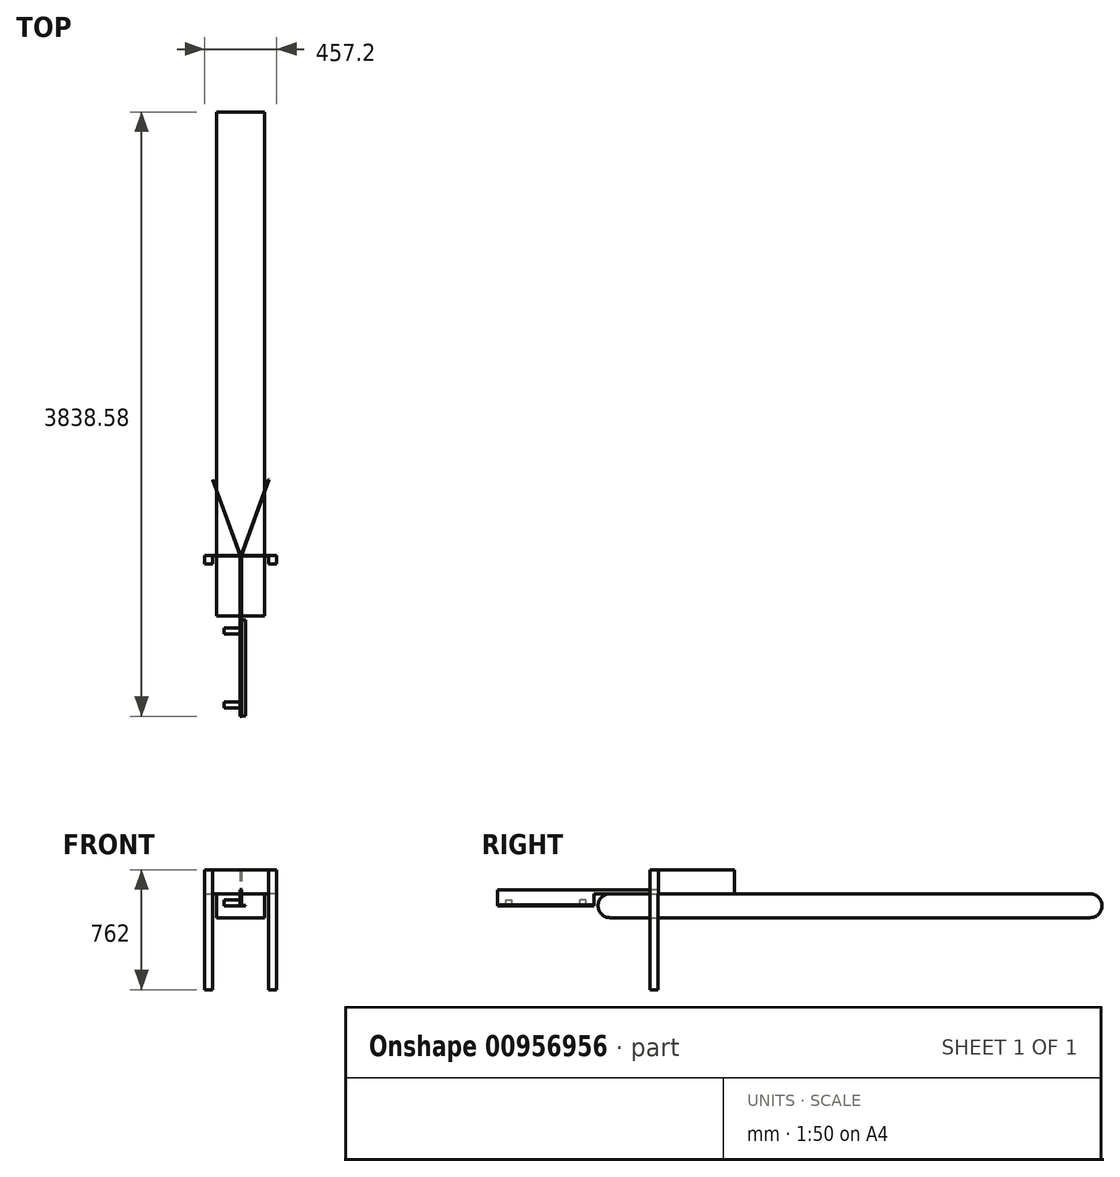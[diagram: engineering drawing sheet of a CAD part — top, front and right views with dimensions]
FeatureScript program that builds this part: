
annotation { "Feature Type Name" : "Feature", "Feature Type Description" : "" }
export const myFeature = defineFeature(function(context is Context, id is Id, definition is map)
    precondition{}
    {
        {
            var Q0;
            Q0=qCreatedBy(makeId("Right.planeOp"),FACE);
            var sketch = newSketch(context, id + "F0", { "sketchPlane" : qUnion([Q0])});
            skLineSegment(sketch, "E0", {"start": v(-1480.5, 76.38) * mm, "end": v(1567.5, 76.38) * mm});
            skLineSegment(sketch, "E1", {"start": v(-1480.5, -76.02) * mm, "end": v(1567.5, -76.02) * mm});
            skArc(sketch, "E2", {"start": v(-1480.5, -76.02) * mm, "mid": v(-1556.7, 0.18) * mm, "end": v(-1480.5, 76.38) * mm});
            skArc(sketch, "E3", {"start": v(1567.5, -76.02) * mm, "mid": v(1643.7, 0.18) * mm, "end": v(1567.5, 76.38) * mm});
            skSolve(sketch);
        }
        {
            var Q0;
            Q0=makeQuery(id+"F0.imprint","IMPRINT",FACE,{"disambiguationData":[TD([[makeQuery(id+"F0.imprint","IMPRINT",EDGE,{"derivedFrom":sQuery(id+"F0.wireOp",EDGE,"E0")}),-1.0]])]});
            extrude(context, id + "F1", {"entities" : qUnion([Q0]), "depth" : 304.8 * mm, "offsetDistance" : 25.4 * mm});
        }
        {
            var Q0;
            Q0=makeQuery(id+"F1.opExtrude","SWEPT_FACE",FACE,{"disambiguationData":[OSD([sQuery(id+"F0.wireOp",EDGE,"E0")])]});
            var sketch = newSketch(context, id + "F2", { "sketchPlane" : qUnion([Q0])});
            skLineSegment(sketch, "E4.bottom", {"start": v(381, -1175.7) * mm, "end": v(152.4, -1175.7) * mm});
            skLineSegment(sketch, "E4.top", {"start": v(381, -1173.4) * mm, "end": v(152.4, -1173.4) * mm});
            skLineSegment(sketch, "E4.left", {"start": v(381, -1175.7) * mm, "end": v(381, -1173.4) * mm});
            skLineSegment(sketch, "E4.right", {"start": v(152.4, -1175.7) * mm, "end": v(152.4, -1173.4) * mm});
            skLineSegment(sketch, "E5", {"start": v(152.4, -1480.5) * mm, "end": v(152.4, 1567.5) * mm, "construction": true});
            skLineSegment(sketch, "E6.bottom", {"start": v(381, -1175.7) * mm, "end": v(330.2, -1175.7) * mm});
            skLineSegment(sketch, "E6.top", {"start": v(381, -1226.5) * mm, "end": v(330.2, -1226.5) * mm});
            skLineSegment(sketch, "E6.left", {"start": v(381, -1175.7) * mm, "end": v(381, -1226.5) * mm});
            skLineSegment(sketch, "E6.right", {"start": v(330.2, -1175.7) * mm, "end": v(330.2, -1226.5) * mm});
            skLineSegment(sketch, "E7", {"start": v(154.43, -1173.4) * mm, "end": v(330.2, -690.49) * mm});
            skLineSegment(sketch, "E8", {"start": v(330.2, -690.49) * mm, "end": v(332.35, -691.27) * mm});
            skLineSegment(sketch, "E9", {"start": v(332.35, -691.27) * mm, "end": v(156.86, -1173.4) * mm});
            skSolve(sketch);
        }
        {
            var Q0;
            {var subQ0=sQuery(id+"F2.wireOp",EDGE,"E4.left");Q0=makeQuery(id+"F2.imprint","IMPRINT",FACE,{"disambiguationData":[TD([[makeQuery(id+"F2.imprint","IMPRINT",EDGE,{"derivedFrom":subQ0}),1.0]])]});}
            var Q1;
            {var subQ5=sQuery(id+"F2.wireOp",EDGE,"E4.right");Q1=makeQuery(id+"F2.imprint","IMPRINT",FACE,{"disambiguationData":[TD([[makeQuery(id+"F2.imprint","IMPRINT",EDGE,{"derivedFrom":subQ5}),-1.0]])]});}
            var Q2;
            {var subQ0=sQuery(id+"F2.wireOp",EDGE,"E8");Q2=makeQuery(id+"F2.imprint","IMPRINT",FACE,{"disambiguationData":[TD([[makeQuery(id+"F2.imprint","IMPRINT",EDGE,{"derivedFrom":subQ0}),-1.0]])]});}
            var Q3;
            {var subQ0=sQuery(id+"F2.wireOp",EDGE,"E7");var subQ1=sQuery(id+"F2.wireOp",EDGE,"E4.top");var subQ2=makeQuery(id+"F2.imprint","INTERSECT",VERTEX,{"derivedFrom":[subQ1,subQ0]});Q3=makeQuery(id+"F2.imprint","IMPRINT",FACE,{"disambiguationData":[TD([[makeQuery(id+"F2.imprint","IMPRINT",EDGE,{"disambiguationData":[TD([[subQ2,1.0]])],"derivedFrom":subQ1}),-1.0]])]});}
            extrude(context, id + "F3", {"entities" : qUnion([Q0, Q1, Q2, Q3]), "operationType" : NewBodyOperationType.ADD, "depth" : 152.4 * mm, "offsetDistance" : 25.4 * mm});
        }
        {
            var Q0;
            Q0=makeQuery(id+"F2.imprint","IMPRINT",FACE,{"disambiguationData":[TD([[makeQuery(id+"F2.imprint","IMPRINT",EDGE,{"derivedFrom":sQuery(id+"F2.wireOp",EDGE,"E6.top")}),-1.0]])]});
            extrude(context, id + "F4", {"entities" : qUnion([Q0]), "operationType" : NewBodyOperationType.ADD, "depth" : 152.4 * mm, "offsetDistance" : 25.4 * mm, "hasSecondDirection" : true, "secondDirectionOppositeDirection" : true, "secondDirectionDepth" : 609.6 * mm});
        }
        {
            var Q0;
            Q0=makeQuery(id+"F1.opExtrude","SWEPT_EDGE",EDGE,{"disambiguationData":[OSD([sQuery(id+"F0.wireOp",EDGE,"E0"),sQuery(id+"F0.wireOp",EDGE,"E2")])]});
            cPoint(context, id + "F5", {"entities" : qUnion([Q0]), "parameter" : 0.5});
        }
        {
            var Q0;
            Q0 = qCreatedBy(id + "F5" ,VERTEX);
            var Q1;
            Q1=makeQuery(id+"F1.opExtrude","SWEPT_EDGE",EDGE,{"disambiguationData":[OSD([sQuery(id+"F0.wireOp",EDGE,"E0"),sQuery(id+"F0.wireOp",EDGE,"E2")])]});
            cPlane(context, id + "F6", {"entities" : qUnion([Q0, Q1]), "cplaneType" : CPlaneType.LINE_POINT, "offset" : 25.4 * mm, "width" : 152.4 * mm, "height" : 152.4 * mm});
        }
        {
            var Q0;
            Q0=makeQuery(id+"F1.opExtrude","SWEPT_BODY",BODY,{"disambiguationData":[OSD([sQuery(id+"F0.wireOp",EDGE,"E0"),sQuery(id+"F0.wireOp",EDGE,"E1"),sQuery(id+"F0.wireOp",EDGE,"E2"),sQuery(id+"F0.wireOp",EDGE,"E3")])]});
            var Q1;
            Q1=qCreatedBy(id+"F6.planeOp",FACE);
            mirror(context, id + "F7", {"operationType" : NewBodyOperationType.ADD, "entities" : qUnion([Q0]), "mirrorPlane" : qUnion([Q1])});
        }
        {
            var Q0;
            {var subQ0=sQuery(id+"F2.wireOp",EDGE,"E4.top");Q0=makeQuery(id+"F7.opPattern","COPY",FACE,{"derivedFrom":makeQuery(id+"F3.opExtrude","SWEPT_FACE",FACE,{"disambiguationData":[OSD([subQ0]),TDD([makeQuery(id+"F2.imprint","IMPRINT",EDGE,{"disambiguationData":[TD([[makeQuery(id+"F2.imprint","INTERSECT",VERTEX,{"derivedFrom":[subQ0,sQuery(id+"F2.wireOp",EDGE,"E4.left")]}),-1.0]])],"derivedFrom":subQ0}),makeQuery(id+"F2.imprint","IMPRINT",EDGE,{"disambiguationData":[TD([[makeQuery(id+"F2.imprint","INTERSECT",VERTEX,{"derivedFrom":[subQ0,sQuery(id+"F2.wireOp",EDGE,"E9")]}),1.0]])],"derivedFrom":subQ0})])]}),"instanceName":"1"});}
            var sketch = newSketch(context, id + "F8", { "sketchPlane" : qUnion([Q0])});
            skLineSegment(sketch, "E10.bottom", {"start": v(-154.43, 76.38) * mm, "end": v(-150.37, 76.38) * mm});
            skLineSegment(sketch, "E10.top", {"start": v(-154.43, 78.92) * mm, "end": v(-150.37, 78.92) * mm});
            skLineSegment(sketch, "E10.left", {"start": v(-154.43, 76.38) * mm, "end": v(-154.43, 78.92) * mm});
            skLineSegment(sketch, "E10.right", {"start": v(-150.37, 76.38) * mm, "end": v(-150.37, 78.92) * mm});
            skSolve(sketch);
        }
        {
            var Q0;
            Q0=makeQuery(id+"F8.imprint","IMPRINT",FACE,{"disambiguationData":[TD([[makeQuery(id+"F8.imprint","IMPRINT",EDGE,{"derivedFrom":sQuery(id+"F8.wireOp",EDGE,"E10.bottom")}),1.0]])]});
            var Q1;
            {var subQ0=makeQuery(id+"F3.opExtrude","SWEPT_FACE",FACE,{"disambiguationData":[OSD([sQuery(id+"F2.wireOp",EDGE,"E4.bottom")])]});Q1=makeQuery(id+"F7.boolean.opBoolean","MERGE",FACE,{"derivedFrom":[subQ0,makeQuery(id+"F7.opPattern","COPY",FACE,{"derivedFrom":subQ0,"instanceName":"1"})]});}
            extrude(context, id + "F9", {"entities" : qUnion([Q0]), "operationType" : NewBodyOperationType.REMOVE, "endBound" : BoundingType.UP_TO_SURFACE, "oppositeDirection" : true, "depth" : 25.4 * mm, "endBoundEntityFace" : qUnion([Q1]), "offsetDistance" : 25.4 * mm});
        }
        {
            var Q0;
            {var subQ6=sQuery(id+"F2.wireOp",EDGE,"E4.right");Q0=makeQuery(id+"F2.imprint","IMPRINT",FACE,{"disambiguationData":[TD([[makeQuery(id+"F2.imprint","IMPRINT",EDGE,{"derivedFrom":subQ6}),1.0]])]});}
            var sketch = newSketch(context, id + "F10", { "sketchPlane" : qUnion([Q0])});
            skLineSegment(sketch, "E11.bottom", {"start": v(150.37, -1175.7) * mm, "end": v(147.2, -1175.7) * mm});
            skLineSegment(sketch, "E11.top", {"start": v(150.37, -1582.1) * mm, "end": v(147.2, -1582.1) * mm});
            skLineSegment(sketch, "E11.left", {"start": v(150.37, -1175.7) * mm, "end": v(150.37, -1582.1) * mm});
            skLineSegment(sketch, "E11.right", {"start": v(147.2, -1175.7) * mm, "end": v(147.2, -1582.1) * mm});
            skLineSegment(sketch, "E12.bottom", {"start": v(154.43, -1175.7) * mm, "end": v(157.6, -1175.7) * mm});
            skLineSegment(sketch, "E12.top", {"start": v(154.43, -1582.1) * mm, "end": v(157.6, -1582.1) * mm});
            skLineSegment(sketch, "E12.left", {"start": v(154.43, -1175.7) * mm, "end": v(154.43, -1582.1) * mm});
            skLineSegment(sketch, "E12.right", {"start": v(157.6, -1175.7) * mm, "end": v(157.6, -1582.1) * mm});
            skSolve(sketch);
        }
        {
            var Q0;
            {var subQ0=sQuery(id+"F10.wireOp",EDGE,"E12.bottom");Q0=makeQuery(id+"F10.imprint","IMPRINT",FACE,{"disambiguationData":[TD([[makeQuery(id+"F10.imprint","IMPRINT",EDGE,{"derivedFrom":subQ0}),1.0]])]});}
            var Q1;
            {var subQ0=sQuery(id+"F10.wireOp",EDGE,"E11.bottom");Q1=makeQuery(id+"F10.imprint","IMPRINT",FACE,{"disambiguationData":[TD([[makeQuery(id+"F10.imprint","IMPRINT",EDGE,{"derivedFrom":subQ0}),1.0]])]});}
            var Q2;
            {var subQ0=sQuery(id+"F10.wireOp",EDGE,"E12.top");Q2=makeQuery(id+"F10.imprint","IMPRINT",FACE,{"disambiguationData":[TD([[makeQuery(id+"F10.imprint","IMPRINT",EDGE,{"derivedFrom":subQ0}),1.0]])]});}
            var Q3;
            {var subQ0=sQuery(id+"F10.wireOp",EDGE,"E11.top");Q3=makeQuery(id+"F10.imprint","IMPRINT",FACE,{"disambiguationData":[TD([[makeQuery(id+"F10.imprint","IMPRINT",EDGE,{"derivedFrom":subQ0}),-1.0]])]});}
            extrude(context, id + "F11", {"entities" : qUnion([Q0, Q1, Q2, Q3]), "operationType" : NewBodyOperationType.ADD, "depth" : 25.4 * mm, "offsetDistance" : 25.4 * mm});
        }
        {
            var Q0;
            Q0=qCreatedBy(makeId("Top.planeOp"),FACE);
            var sketch = newSketch(context, id + "F12", { "sketchPlane" : qUnion([Q0])});
            skLineSegment(sketch, "E13.bottom", {"start": v(150.37, -1582.1) * mm, "end": v(147.2, -1582.1) * mm});
            skLineSegment(sketch, "E13.top", {"start": v(150.37, -2191.7) * mm, "end": v(147.2, -2191.7) * mm});
            skLineSegment(sketch, "E13.left", {"start": v(150.37, -1582.1) * mm, "end": v(150.37, -2191.7) * mm});
            skLineSegment(sketch, "E13.right", {"start": v(147.2, -1582.1) * mm, "end": v(147.2, -2191.7) * mm});
            skLineSegment(sketch, "E14.bottom", {"start": v(154.43, -1582.1) * mm, "end": v(157.6, -1582.1) * mm});
            skLineSegment(sketch, "E14.top", {"start": v(154.43, -2191.7) * mm, "end": v(157.6, -2191.7) * mm});
            skLineSegment(sketch, "E14.left", {"start": v(154.43, -1582.1) * mm, "end": v(154.43, -2191.7) * mm});
            skLineSegment(sketch, "E14.right", {"start": v(157.6, -1582.1) * mm, "end": v(157.6, -2191.7) * mm});
            skLineSegment(sketch, "E15", {"start": v(154.43, -1582.1) * mm, "end": v(150.37, -1582.1) * mm});
            skLineSegment(sketch, "E16", {"start": v(150.37, -2191.7) * mm, "end": v(154.43, -2191.7) * mm});
            skLineSegment(sketch, "E17.bottom", {"start": v(147.2, -2191.7) * mm, "end": v(157.6, -2191.7) * mm});
            skLineSegment(sketch, "E17.top", {"start": v(147.2, -2194.87) * mm, "end": v(157.6, -2194.87) * mm});
            skLineSegment(sketch, "E17.left", {"start": v(147.2, -2191.7) * mm, "end": v(147.2, -2194.87) * mm});
            skLineSegment(sketch, "E17.right", {"start": v(157.6, -2191.7) * mm, "end": v(157.6, -2194.87) * mm});
            skLineSegment(sketch, "E18.bottom", {"start": v(157.6, -1582.1) * mm, "end": v(183, -1582.1) * mm});
            skLineSegment(sketch, "E18.top", {"start": v(157.6, -2191.7) * mm, "end": v(183, -2191.7) * mm});
            skLineSegment(sketch, "E18.right", {"start": v(183, -1582.1) * mm, "end": v(183, -2191.7) * mm});
            skSolve(sketch);
        }
        {
            var Q0;
            Q0=makeQuery(id+"F12.imprint","IMPRINT",FACE,{"disambiguationData":[TD([[makeQuery(id+"F12.imprint","IMPRINT",EDGE,{"derivedFrom":sQuery(id+"F12.wireOp",EDGE,"E13.bottom")}),1.0]])]});
            var Q1;
            Q1=makeQuery(id+"F12.imprint","IMPRINT",FACE,{"disambiguationData":[TD([[makeQuery(id+"F12.imprint","IMPRINT",EDGE,{"derivedFrom":sQuery(id+"F12.wireOp",EDGE,"E14.bottom")}),-1.0]])]});
            var Q2;
            Q2=makeQuery(id+"F12.imprint","IMPRINT",FACE,{"disambiguationData":[TD([[makeQuery(id+"F12.imprint","IMPRINT",EDGE,{"derivedFrom":sQuery(id+"F12.wireOp",EDGE,"E17.top")}),1.0]])]});
            extrude(context, id + "F13", {"entities" : qUnion([Q0, Q1, Q2]), "operationType" : NewBodyOperationType.ADD, "depth" : 101.6 * mm, "offsetDistance" : 25.4 * mm});
        }
        {
            var Q0;
            Q0=makeQuery(id+"F12.imprint","IMPRINT",FACE,{"disambiguationData":[TD([[makeQuery(id+"F12.imprint","IMPRINT",EDGE,{"derivedFrom":sQuery(id+"F12.wireOp",EDGE,"E13.left")}),1.0]])]});
            var Q1;
            Q1=makeQuery(id+"F12.imprint","IMPRINT",FACE,{"disambiguationData":[TD([[makeQuery(id+"F12.imprint","IMPRINT",EDGE,{"derivedFrom":sQuery(id+"F12.wireOp",EDGE,"E18.bottom")}),-1.0]])]});
            var Q2;
            Q2=makeQuery(id+"F12.imprint","IMPRINT",FACE,{"disambiguationData":[TD([[makeQuery(id+"F12.imprint","IMPRINT",EDGE,{"derivedFrom":sQuery(id+"F12.wireOp",EDGE,"E14.bottom")}),-1.0]])]});
            extrude(context, id + "F14", {"entities" : qUnion([Q0, Q1, Q2]), "operationType" : NewBodyOperationType.ADD, "depth" : 2.3 * mm, "offsetDistance" : 25.4 * mm});
        }
        {
            var Q0;
            Q0=makeQuery(id+"F13.opExtrude","SWEPT_FACE",FACE,{"disambiguationData":[OSD([sQuery(id+"F12.wireOp",EDGE,"E13.right"),sQuery(id+"F12.wireOp",EDGE,"E17.left")])]});
            var sketch = newSketch(context, id + "F15", { "sketchPlane" : qUnion([Q0])});
            skLineSegment(sketch, "E19.bottom", {"start": v(2140.9, 0) * mm, "end": v(2102.8, 0) * mm});
            skLineSegment(sketch, "E19.top", {"start": v(2140.9, 38.1) * mm, "end": v(2102.8, 38.1) * mm});
            skLineSegment(sketch, "E19.left", {"start": v(2140.9, 0) * mm, "end": v(2140.9, 38.1) * mm});
            skLineSegment(sketch, "E19.right", {"start": v(2102.8, 0) * mm, "end": v(2102.8, 38.1) * mm});
            skLineSegment(sketch, "E20.bottom", {"start": v(1632.9, 0) * mm, "end": v(1671, 0) * mm});
            skLineSegment(sketch, "E20.top", {"start": v(1632.9, 38.1) * mm, "end": v(1671, 38.1) * mm});
            skLineSegment(sketch, "E20.left", {"start": v(1632.9, 0) * mm, "end": v(1632.9, 38.1) * mm});
            skLineSegment(sketch, "E20.right", {"start": v(1671, 0) * mm, "end": v(1671, 38.1) * mm});
            skLineSegment(sketch, "E21.bottom", {"start": v(1867.84, 0) * mm, "end": v(1905.94, 0) * mm});
            skLineSegment(sketch, "E21.top", {"start": v(1867.84, 38.1) * mm, "end": v(1905.94, 38.1) * mm});
            skLineSegment(sketch, "E21.left", {"start": v(1867.84, 0) * mm, "end": v(1867.84, 38.1) * mm});
            skLineSegment(sketch, "E21.right", {"start": v(1905.94, 0) * mm, "end": v(1905.94, 38.1) * mm});
            skLineSegment(sketch, "E22", {"start": v(1582.1, 0) * mm, "end": v(1632.9, 0) * mm, "construction": true});
            skLineSegment(sketch, "E23", {"start": v(1671, 0) * mm, "end": v(1867.84, 0) * mm, "construction": true});
            skLineSegment(sketch, "E24", {"start": v(1905.94, 0) * mm, "end": v(2102.8, 0) * mm, "construction": true});
            skLineSegment(sketch, "E25", {"start": v(2140.9, 0) * mm, "end": v(2191.7, 0) * mm, "construction": true});
            skSolve(sketch);
        }
        {
            var Q0;
            Q0=makeQuery(id+"F15.imprint","IMPRINT",FACE,{"disambiguationData":[TD([[makeQuery(id+"F15.imprint","IMPRINT",EDGE,{"derivedFrom":sQuery(id+"F15.wireOp",EDGE,"E20.bottom")}),1.0]])]});
            var Q1;
            Q1=makeQuery(id+"F15.imprint","IMPRINT",FACE,{"disambiguationData":[TD([[makeQuery(id+"F15.imprint","IMPRINT",EDGE,{"derivedFrom":sQuery(id+"F15.wireOp",EDGE,"E19.bottom")}),1.0]])]});
            extrude(context, id + "F16", {"entities" : qUnion([Q0, Q1]), "operationType" : NewBodyOperationType.ADD, "depth" : 101.6 * mm, "offsetDistance" : 25.4 * mm});
        }
        {
            var Q0;
            Q0=makeQuery(id+"F13.opExtrude","SWEPT_FACE",FACE,{"disambiguationData":[OSD([sQuery(id+"F12.wireOp",EDGE,"E14.right"),sQuery(id+"F12.wireOp",EDGE,"E17.right")])]});
            var sketch = newSketch(context, id + "F17", { "sketchPlane" : qUnion([Q0])});
            skLineSegment(sketch, "E26.bottom", {"start": v(-2192.58, 2.29) * mm, "end": v(-1582.1, 2.29) * mm});
            skLineSegment(sketch, "E26.top", {"start": v(-2192.58, 4.83) * mm, "end": v(-1582.1, 4.83) * mm});
            skLineSegment(sketch, "E26.left", {"start": v(-2192.58, 2.29) * mm, "end": v(-2192.58, 4.83) * mm});
            skLineSegment(sketch, "E26.right", {"start": v(-1582.1, 2.29) * mm, "end": v(-1582.1, 4.83) * mm});
            skSolve(sketch);
        }
        {
            var Q0;
            Q0=makeQuery(id+"F17.imprint","IMPRINT",FACE,{"disambiguationData":[TD([[makeQuery(id+"F17.imprint","IMPRINT",EDGE,{"derivedFrom":sQuery(id+"F17.wireOp",EDGE,"E26.bottom")}),1.0]])]});
            var Q1;
            Q1=makeQuery(id+"F13.opExtrude","SWEPT_FACE",FACE,{"disambiguationData":[OSD([sQuery(id+"F12.wireOp",EDGE,"E14.left")])]});
            extrude(context, id + "F18", {"entities" : qUnion([Q0]), "operationType" : NewBodyOperationType.REMOVE, "endBound" : BoundingType.UP_TO_SURFACE, "oppositeDirection" : true, "depth" : 25.4 * mm, "endBoundEntityFace" : qUnion([Q1]), "offsetDistance" : 25.4 * mm});
        }
    });
